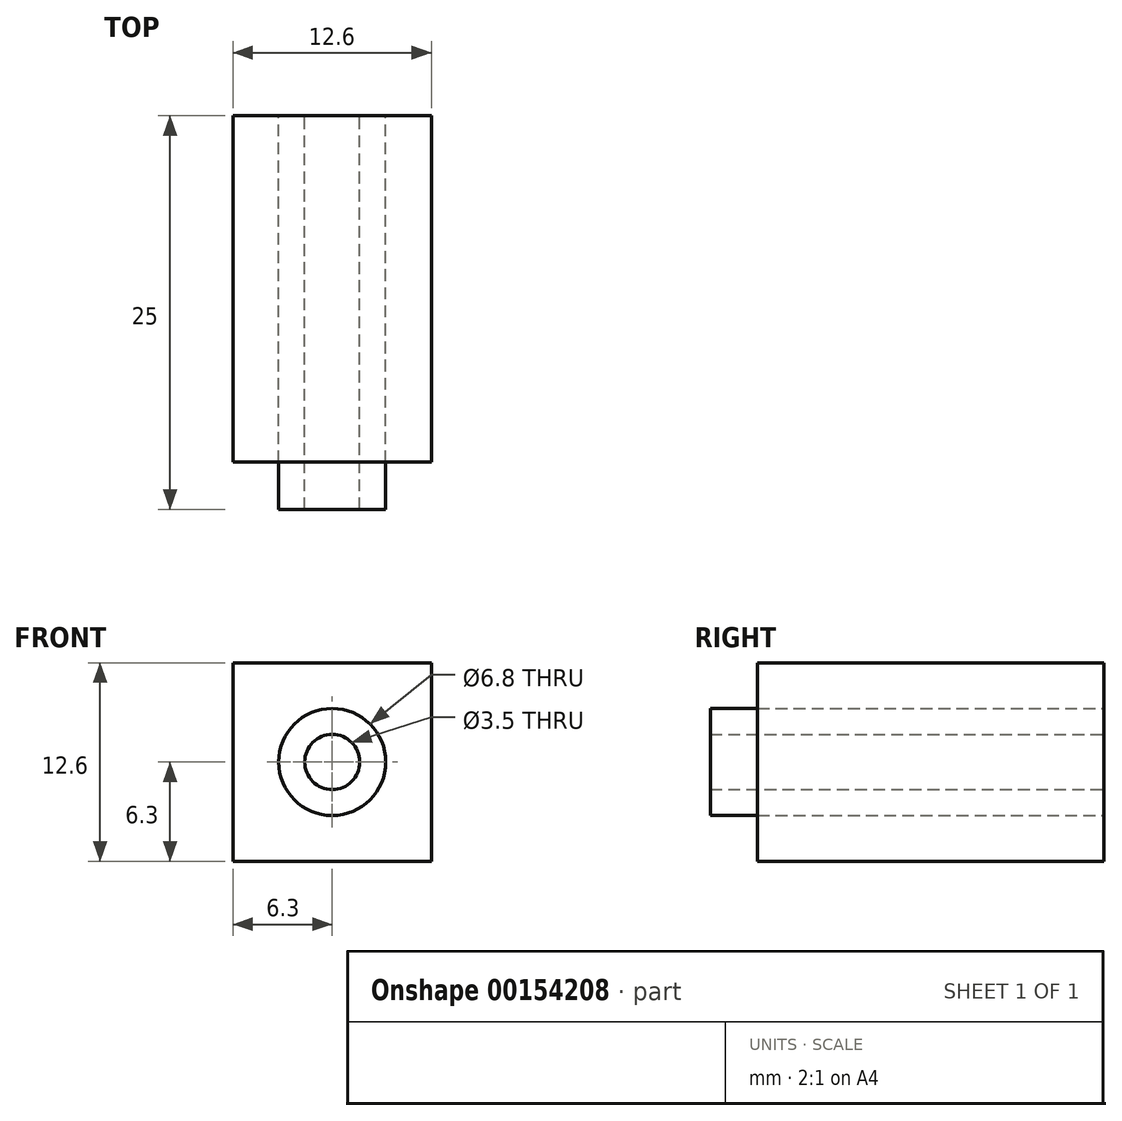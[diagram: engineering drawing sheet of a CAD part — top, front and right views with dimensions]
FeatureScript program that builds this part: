
annotation { "Feature Type Name" : "Feature", "Feature Type Description" : "" }
export const myFeature = defineFeature(function(context is Context, id is Id, definition is map)
    precondition{}
    {
        {
            var Q0;
            Q0=qCreatedBy(makeId("Front.planeOp"),FACE);
            var sketch = newSketch(context, id + "F0", { "sketchPlane" : qUnion([Q0])});
            skPoint(sketch, "E0.middle", {"position": v(0, 0) * mm});
            skCircle(sketch, "E1", {"center": v(0, 0) * mm, "radius": 3.4 * mm});
            skCircle(sketch, "E2", {"center": v(0, 0) * mm, "radius": 1.75 * mm});
            skLineSegment(sketch, "E3.bottom", {"start": v(6.3, 6.3) * mm, "end": v(-6.3, 6.3) * mm});
            skLineSegment(sketch, "E3.top", {"start": v(6.3, -6.3) * mm, "end": v(-6.3, -6.3) * mm});
            skLineSegment(sketch, "E3.left", {"start": v(6.3, 6.3) * mm, "end": v(6.3, -6.3) * mm});
            skLineSegment(sketch, "E3.right", {"start": v(-6.3, 6.3) * mm, "end": v(-6.3, -6.3) * mm});
            skLineSegment(sketch, "E4", {"start": v(-3.3, 6.3) * mm, "end": v(-3.3, 4.3) * mm});
            skLineSegment(sketch, "E5", {"start": v(-6.3, 4.31) * mm, "end": v(-3.3, 4.3) * mm});
            skLineSegment(sketch, "E6", {"start": v(6.3, -4.3) * mm, "end": v(2.8, -4.3) * mm});
            skLineSegment(sketch, "E7", {"start": v(2.8, -4.3) * mm, "end": v(2.8, -6.3) * mm});
            skSolve(sketch);
        }
        {
            var Q0;
            Q0=makeQuery(id+"F0.imprint","IMPRINT",FACE,{"disambiguationData":[TD([[makeQuery(id+"F0.imprint","IMPRINT",EDGE,{"derivedFrom":sQuery(id+"F0.wireOp",EDGE,"E1")}),1.0]])]});
            extrude(context, id + "F1", {"entities" : qUnion([Q0]), "depth" : 25 * mm});
        }
        {
            var Q0;
            Q0 = qSketchRegion(id + "F0", true);
            var Q1;
            Q1=sQuery(id+"F0.wireOp",EDGE,"ioPqL0WC-Yldx-j6MJ-tCip-UG3mjgeliYek");
            var Q2;
            Q2=sQuery(id+"F0.wireOp",EDGE,"fN74aVpr-T7IU-Hicq-o8vV-IscqzfNMs8t8");
            var Q3;
            Q3=sQuery(id+"F0.wireOp",EDGE,"GqAEQXM0-VvW7-0elj-3Hcr-YP5t0uZKxZkH");
            var Q4;
            Q4=sQuery(id+"F0.wireOp",EDGE,"KDgUB6K5-Tyce-oIvw-cPVa-unY0vvR6rh6F");
            var Q5;
            Q5=sQuery(id+"F0.wireOp",EDGE,"gZayc3kM-6v7S-Zlbf-S7Jr-kmsQqtWeCda4");
            var Q6;
            Q6=sQuery(id+"F0.wireOp",EDGE,"IO1lTRie-FjSc-HII2-fFNK-rfN2eRhQkT0d");
            var Q7;
            Q7=sQuery(id+"F0.wireOp",EDGE,"EigLiQHa-fHr6-zMoU-EhQQ-XHv0tgRitlyy");
            var Q8;
            Q8=sQuery(id+"F0.wireOp",EDGE,"0DlGtXJW-pLfc-K6Aq-Wk9w-UzqVdFCBHpax");
            var Q9;
            Q9=sQuery(id+"F0.wireOp",EDGE,"E1");
            extrude(context, id + "F2", {"entities" : qUnion([Q0]), "surfaceEntities" : qUnion([Q1, Q2, Q3, Q4, Q5, Q6, Q7, Q8, Q9]), "depth" : 22 * mm});
        }
    });
